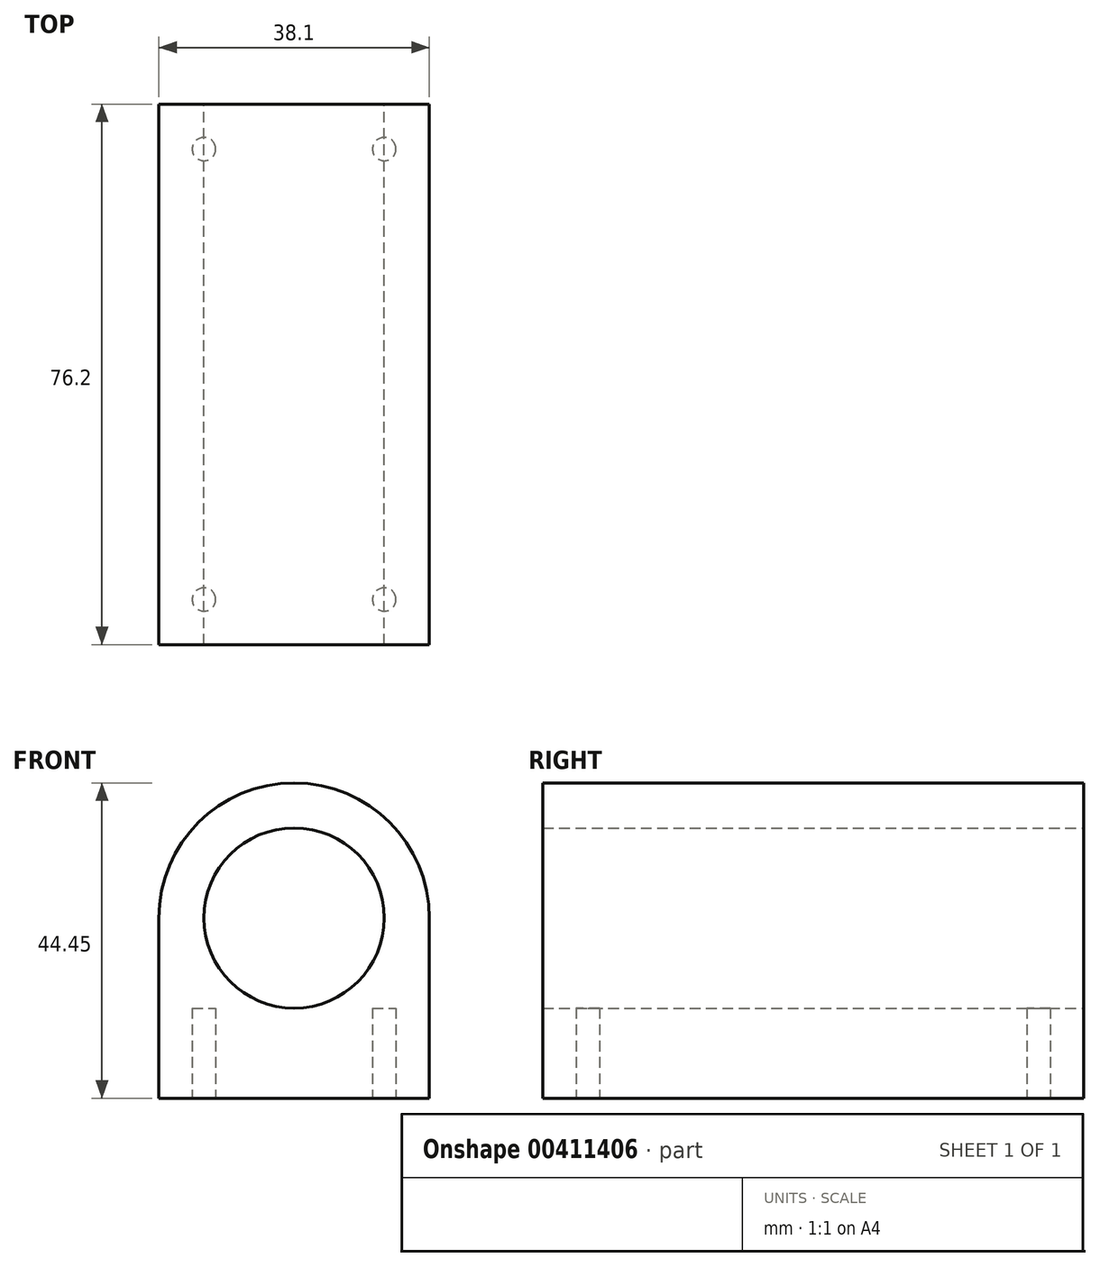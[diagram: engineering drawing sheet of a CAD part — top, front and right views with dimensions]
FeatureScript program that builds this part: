
annotation { "Feature Type Name" : "Feature", "Feature Type Description" : "" }
export const myFeature = defineFeature(function(context is Context, id is Id, definition is map)
    precondition{}
    {
        {
            var Q0;
            Q0=qCreatedBy(makeId("Front.planeOp"),FACE);
            var sketch = newSketch(context, id + "F0", { "sketchPlane" : qUnion([Q0])});
            skArc(sketch, "E0", {"start": v(19.05, 0) * mm, "mid": v(0, 19.05) * mm, "end": v(-19.05, 0) * mm});
            skLineSegment(sketch, "E1.top", {"start": v(-19.05, -25.4) * mm, "end": v(19.05, -25.4) * mm});
            skLineSegment(sketch, "E1.left", {"start": v(-19.05, 0) * mm, "end": v(-19.05, -25.4) * mm});
            skLineSegment(sketch, "E1.right", {"start": v(19.05, 0) * mm, "end": v(19.05, -25.4) * mm});
            skCircle(sketch, "E2", {"center": v(0, 0) * mm, "radius": 12.7 * mm});
            skSolve(sketch);
        }
        {
            var Q0;
            Q0 = qSketchRegion(id + "F0", true);
            extrude(context, id + "F1", {"entities" : qUnion([Q0]), "depth" : 76.2 * mm});
        }
        {
            var Q0;
            Q0=makeQuery(id+"F1.opExtrude","SWEPT_FACE",FACE,{"disambiguationData":[OSD([sQuery(id+"F0.wireOp",EDGE,"E1.top")])]});
            var sketch = newSketch(context, id + "F2", { "sketchPlane" : qUnion([Q0])});
            skCircle(sketch, "E3", {"center": v(-12.7, 69.85) * mm, "radius": 1.65 * mm});
            skCircle(sketch, "E4", {"center": v(12.7, 69.85) * mm, "radius": 1.65 * mm});
            skCircle(sketch, "E5", {"center": v(-12.7, 6.35) * mm, "radius": 1.65 * mm});
            skCircle(sketch, "E6", {"center": v(12.7, 6.35) * mm, "radius": 1.65 * mm});
            skSolve(sketch);
        }
        {
            var Q0;
            Q0 = qSketchRegion(id + "F2", true);
            extrude(context, id + "F3", {"entities" : qUnion([Q0]), "operationType" : NewBodyOperationType.REMOVE, "oppositeDirection" : true, "depth" : 12.7 * mm});
        }
    });
